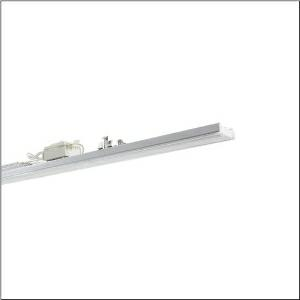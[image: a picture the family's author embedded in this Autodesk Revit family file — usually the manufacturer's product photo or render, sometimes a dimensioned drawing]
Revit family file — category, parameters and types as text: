
# Revit family: licross_r__21_recessed_ho_52te18cn4c5m_57f1
name_source: partatom
category: Lighting Fixtures
units: mm (PartAtom-declared; Revit-internal decimal feet)

## family parameters
Cut with Voids When Loaded = No
Host = Face
Light Source = No
Part Type = Normal
Room Calculation Point = No
Round Connector Dimension = Use Diameter
Shared = No

## types (1)
- --- (1 x LED, 12540 lm, 68.4 W, 4000K)
    Apparent Load = 68 VA
    CIE Flux Codes = 75 94 99 100 100
    Color Rendering = 80
    Color Temperature = 4000K
    Default Elevation = 1800 mm
    Description = Licross® 21 Recessed HO, luminaire insert, of sheet steel, galvanised, coil coated, white, length: 1.500mm, width: 66mm, height: 67mm, LED rated luminous flux: 12.540lm, light colour: 840, control gear: ON/OFF Multilumen, CLOi, control gear: ECG Multilumen, with plug, 3-pole, with phase selection, mains connection: 220..240V, AC, 50/60Hz, start of lifetime: 68W, end of service life: 83W, internal wiring halogen-free, primary light control with lens, of plastic, primary optical cover: cover, of PMMA, light emission: direct distribution, primary light characteristic: symmetric, protection rating (complete): IP54, insulation class (complete): insulation class I (protective earthing), certification: CE, ENEC, VDE, UKCA, protection symbol: D if used in an environment with non-conductive dust loads with corresponding accessories, impact resistance: IK06, permissible ambient temperature for indoor applications: -35..+30°C, corresponds to IFS (International Featured Standards) requirements for safety and quality in the food industry, reducing of maximum allowable ambient temperature of 5°C with ceiling mounting, LABS conformity tested according to VDMA 24364:2018-05, packaging unit: 1 piece
    Height = 58 mm
    Lamp = 1 x LED
    Lamp Light Flux = 12540 lm
    Lamp Power = 68.4 W
    Lamp count = 1
    Length = 1500 mm
    Luminous efficacy = 183 lm/W
    Manufacturer = Siteco
    ModVariant = No
    Model = 52TE18CN4C5M
    Mounting Place = Ceiling
    Mounting Type = Pendant
    Number of Poles = 1
    OnlyDefault = Yes
    Power Factor = 1
    Product Name = Licross® 21 Recessed HO
    Product group = luminaire insert | ceiling pendant
    ProductGroupID = 902
    Protection Class = Protection class I
    Protection Degree = IP 54
    RLX_Detail_Level = 1
    RLX_Emergency_Light_Flux = 0 lm
    RLX_Emergency_Type = 0
    RLX_Emergency_Type_DB = No
    RlxData = <blob elided: 22409 chars, md5=feac0d23>
    Socket = socket
    Standby Power = 0 W
    System Light Flux = 12540 lm
    System Power = 68 W
    Type Comments = factory setting: luminous flux: 100 % | (A | C | E) | 161 mA
    Type Image = l_1296930.jpg
    URL = http://relux.com
    VarID = @adj_131419
    Voltage = 0 V
    Weight = 0.00 kg
    Width = 66 mm

## geometry (parser evidence)
native form markers: Blend x4, Sweep x12
no freeform markers — native parametric forms only
